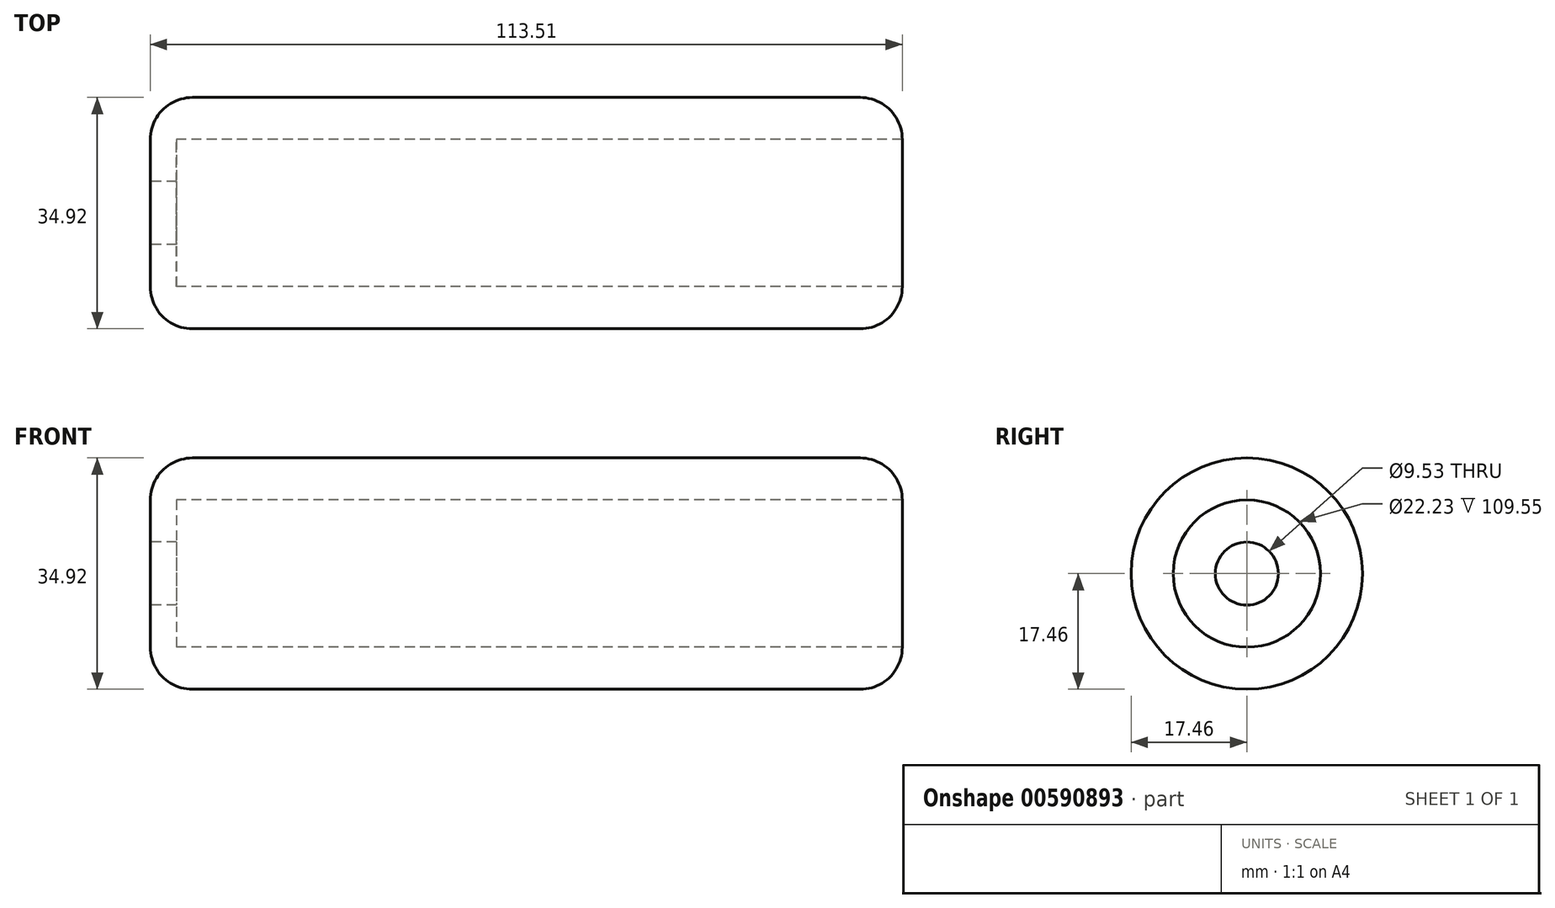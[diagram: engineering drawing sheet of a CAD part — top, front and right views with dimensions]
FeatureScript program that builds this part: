
annotation { "Feature Type Name" : "Feature", "Feature Type Description" : "" }
export const myFeature = defineFeature(function(context is Context, id is Id, definition is map)
    precondition{}
    {
        {
            var Q0;
            Q0=qCreatedBy(makeId("Front.planeOp"),FACE);
            var sketch = newSketch(context, id + "F0", { "sketchPlane" : qUnion([Q0])});
            skLineSegment(sketch, "E0", {"start": v(0, 0) * mm, "end": v(127, 0) * mm, "construction": true});
            skLineSegment(sketch, "E1", {"start": v(0, -4.76) * mm, "end": v(3.96, -4.76) * mm});
            skLineSegment(sketch, "E2", {"start": v(3.96, -4.76) * mm, "end": v(3.96, -11.11) * mm});
            skLineSegment(sketch, "E3", {"start": v(3.96, -11.11) * mm, "end": v(113.51, -11.11) * mm});
            skLineSegment(sketch, "E4", {"start": v(113.51, -11.11) * mm, "end": v(113.51, -17.46) * mm});
            skLineSegment(sketch, "E5", {"start": v(113.51, -17.46) * mm, "end": v(0, -17.46) * mm});
            skLineSegment(sketch, "E6", {"start": v(0, -17.46) * mm, "end": v(0, -4.76) * mm});
            skSolve(sketch);
        }
        {
            var Q0;
            Q0 = qSketchRegion(id + "F0", true);
            var Q1;
            Q1=sQuery(id+"F0.wireOp",EDGE,"E0");
            revolve(context, id + "F1", {"entities" : qUnion([Q0]), "axis" : qUnion([Q1]), "revolveType" : RevolveType.FULL});
        }
        {
            var Q0;
            Q0=makeQuery(id+"F1.opRevolve","SWEPT_EDGE",EDGE,{"disambiguationData":[OSD([sQuery(id+"F0.wireOp",EDGE,"E5"),sQuery(id+"F0.wireOp",EDGE,"E6")])]});
            var Q1;
            Q1=makeQuery(id+"F1.opRevolve","SWEPT_EDGE",EDGE,{"disambiguationData":[OSD([sQuery(id+"F0.wireOp",EDGE,"E4"),sQuery(id+"F0.wireOp",EDGE,"E5")])]});
            fillet(context, id + "F2", {"entities" : qUnion([Q0, Q1]), "radius" : 6.35 * mm, "tangentPropagation" : true, "allowEdgeOverflow" : false});
        }
    });
